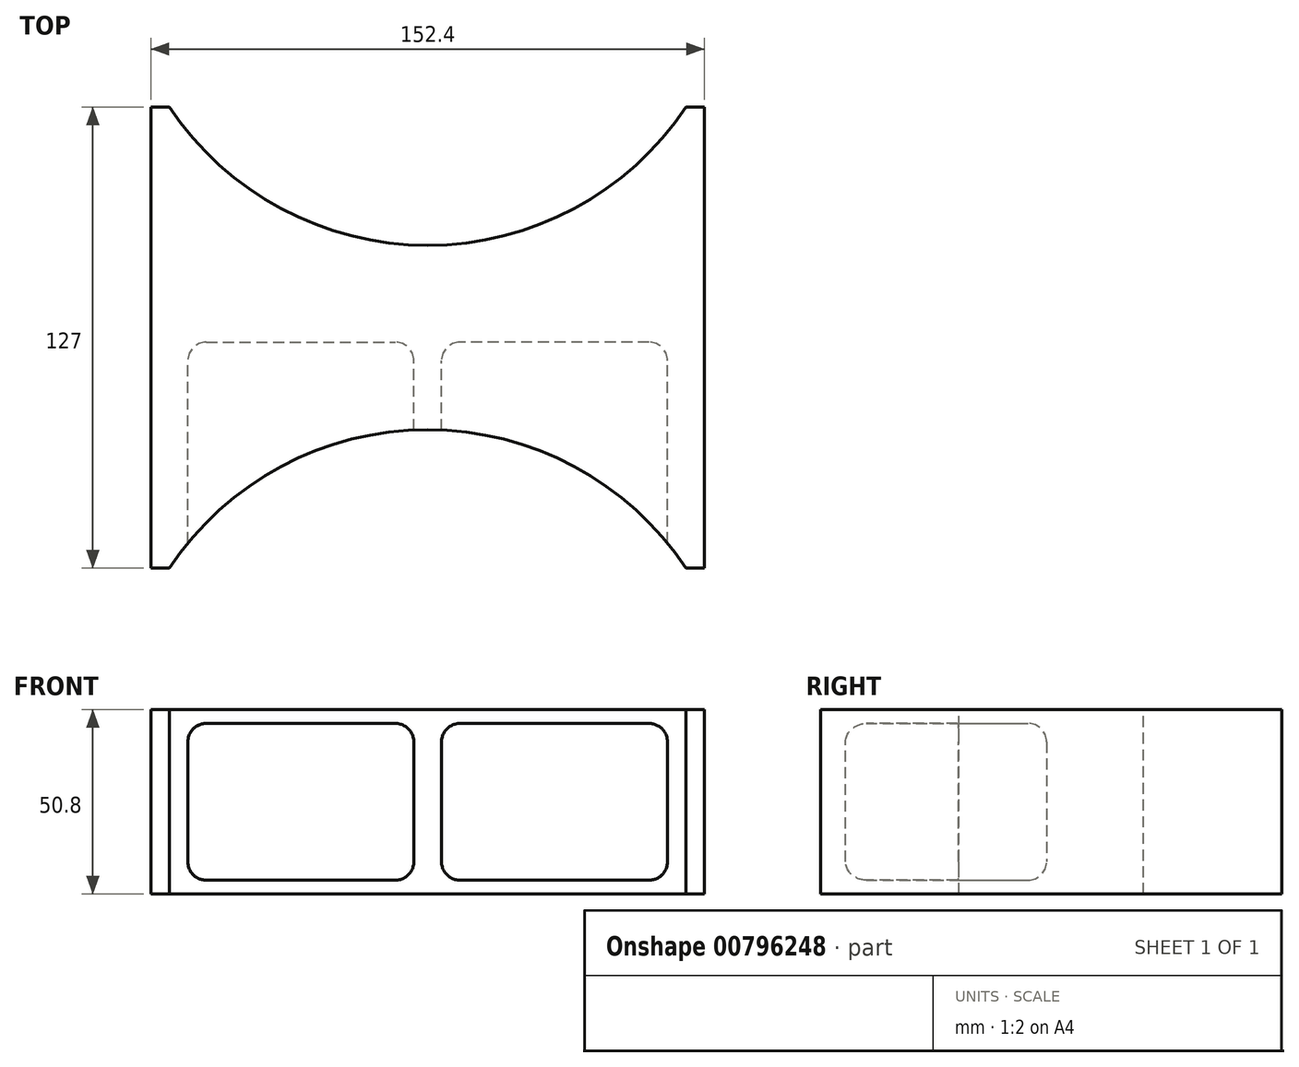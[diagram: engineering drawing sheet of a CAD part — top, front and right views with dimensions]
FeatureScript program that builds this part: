
annotation { "Feature Type Name" : "Feature", "Feature Type Description" : "" }
export const myFeature = defineFeature(function(context is Context, id is Id, definition is map)
    precondition{}
    {
        {
            var Q0;
            Q0=qCreatedBy(makeId("Top.planeOp"),FACE);
            var sketch = newSketch(context, id + "F0", { "sketchPlane" : qUnion([Q0])});
            skLineSegment(sketch, "E0.bottom", {"start": v(76.2, 63.5) * mm, "end": v(-76.2, 63.5) * mm});
            skLineSegment(sketch, "E0.top", {"start": v(76.2, -63.5) * mm, "end": v(-76.2, -63.5) * mm});
            skLineSegment(sketch, "E0.left", {"start": v(76.2, 63.5) * mm, "end": v(76.2, -63.5) * mm});
            skLineSegment(sketch, "E0.right", {"start": v(-76.2, 63.5) * mm, "end": v(-76.2, -63.5) * mm});
            skPoint(sketch, "E0.middle", {"position": v(0, 0) * mm});
            skSolve(sketch);
        }
        {
            var Q0;
            Q0 = qSketchRegion(id + "F0", true);
            extrude(context, id + "F1", {"entities" : qUnion([Q0]), "depth" : 50.8 * mm, "offsetDistance" : 25.4 * mm});
        }
        {
            var Q0;
            Q0=makeQuery(id+"F1.opExtrude","CAP_FACE",FACE,{"disambiguationData":[OSD([sQuery(id+"F0.wireOp",EDGE,"E0.bottom"),sQuery(id+"F0.wireOp",EDGE,"E0.top"),sQuery(id+"F0.wireOp",EDGE,"E0.left"),sQuery(id+"F0.wireOp",EDGE,"E0.right")])],"isStart":false});
            var sketch = newSketch(context, id + "F2", { "sketchPlane" : qUnion([Q0])});
            skArc(sketch, "E1", {"start": v(71.12, -63.5) * mm, "mid": v(0, -25.4) * mm, "end": v(-71.12, -63.5) * mm});
            skArc(sketch, "E2.MirrorCS", {"start": v(71.12, 63.5) * mm, "mid": v(0, 25.4) * mm, "end": v(-71.12, 63.5) * mm});
            skLineSegment(sketch, "E3", {"start": v(-71.12, -63.5) * mm, "end": v(71.12, -63.5) * mm});
            skLineSegment(sketch, "E4", {"start": v(71.12, 63.5) * mm, "end": v(-71.12, 63.5) * mm});
            skSolve(sketch);
        }
        {
            var Q0;
            Q0 = qSketchRegion(id + "F2", true);
            extrude(context, id + "F3", {"entities" : qUnion([Q0]), "operationType" : NewBodyOperationType.REMOVE, "endBound" : BoundingType.THROUGH_ALL, "oppositeDirection" : true, "depth" : 25.4 * mm, "offsetDistance" : 25.4 * mm});
        }
        {
            var Q0;
            Q0=qCreatedBy(makeId("Front.planeOp"),FACE);
            cPlane(context, id + "F4", {"entities" : qUnion([Q0]), "cplaneType" : CPlaneType.OFFSET, "offset" : 1.27 * mm, "width" : 152.4 * mm, "height" : 152.4 * mm});
        }
        {
            var Q0;
            Q0=qCreatedBy(id+"F4.planeOp",FACE);
            var sketch = newSketch(context, id + "F5", { "sketchPlane" : qUnion([Q0])});
            skLineSegment(sketch, "E5.bottom", {"start": v(-66.04, 47) * mm, "end": v(-3.81, 47) * mm});
            skLineSegment(sketch, "E5.top", {"start": v(-66.04, 3.81) * mm, "end": v(-3.8, 3.81) * mm});
            skLineSegment(sketch, "E5.left", {"start": v(-66.04, 47) * mm, "end": v(-66.04, 3.81) * mm});
            skLineSegment(sketch, "E5.right", {"start": v(-3.81, 47) * mm, "end": v(-3.81, 3.81) * mm});
            skLineSegment(sketch, "E6.MirrorCS", {"start": v(66.04, 47) * mm, "end": v(3.81, 47) * mm});
            skLineSegment(sketch, "E7.MirrorCS", {"start": v(3.81, 47) * mm, "end": v(3.81, 3.81) * mm});
            skLineSegment(sketch, "E8.MirrorCS", {"start": v(66.04, 3.81) * mm, "end": v(3.8, 3.81) * mm});
            skLineSegment(sketch, "E9.MirrorCS", {"start": v(66.04, 47) * mm, "end": v(66.04, 3.81) * mm});
            skSolve(sketch);
        }
        {
            var Q0;
            Q0 = qSketchRegion(id + "F5", true);
            extrude(context, id + "F6", {"entities" : qUnion([Q0]), "operationType" : NewBodyOperationType.REMOVE, "endBound" : BoundingType.THROUGH_ALL, "depth" : 25.4 * mm, "offsetDistance" : 25.4 * mm});
        }
        {
            var Q0;
            Q0=makeQuery(id+"F6.boolean.opBoolean","COPY",EDGE,{"derivedFrom":makeQuery(id+"F6.opExtrude","CAP_EDGE",EDGE,{"disambiguationData":[OSD([sQuery(id+"F5.wireOp",EDGE,"E5.right")])],"isStart":true})});
            var Q1;
            Q1=makeQuery(id+"F6.boolean.opBoolean","COPY",EDGE,{"derivedFrom":makeQuery(id+"F6.opExtrude","SWEPT_EDGE",EDGE,{"disambiguationData":[OSD([sQuery(id+"F5.wireOp",EDGE,"E5.top"),sQuery(id+"F5.wireOp",EDGE,"E5.right")])]})});
            var Q2;
            Q2=makeQuery(id+"F6.boolean.opBoolean","COPY",EDGE,{"derivedFrom":makeQuery(id+"F6.opExtrude","CAP_EDGE",EDGE,{"disambiguationData":[OSD([sQuery(id+"F5.wireOp",EDGE,"E5.top")])],"isStart":true})});
            var Q3;
            Q3=makeQuery(id+"F6.boolean.opBoolean","COPY",EDGE,{"derivedFrom":makeQuery(id+"F6.opExtrude","SWEPT_EDGE",EDGE,{"disambiguationData":[OSD([sQuery(id+"F5.wireOp",EDGE,"E5.bottom"),sQuery(id+"F5.wireOp",EDGE,"E5.right")])]})});
            var Q4;
            Q4=makeQuery(id+"F6.boolean.opBoolean","COPY",EDGE,{"derivedFrom":makeQuery(id+"F6.opExtrude","CAP_EDGE",EDGE,{"disambiguationData":[OSD([sQuery(id+"F5.wireOp",EDGE,"E5.bottom")])],"isStart":true})});
            var Q5;
            Q5=makeQuery(id+"F6.boolean.opBoolean","COPY",EDGE,{"derivedFrom":makeQuery(id+"F6.opExtrude","SWEPT_EDGE",EDGE,{"disambiguationData":[OSD([sQuery(id+"F5.wireOp",EDGE,"E5.bottom"),sQuery(id+"F5.wireOp",EDGE,"E5.left")])]})});
            var Q6;
            Q6=makeQuery(id+"F6.boolean.opBoolean","COPY",EDGE,{"derivedFrom":makeQuery(id+"F6.opExtrude","CAP_EDGE",EDGE,{"disambiguationData":[OSD([sQuery(id+"F5.wireOp",EDGE,"E5.left")])],"isStart":true})});
            var Q7;
            Q7=makeQuery(id+"F6.boolean.opBoolean","COPY",EDGE,{"derivedFrom":makeQuery(id+"F6.opExtrude","SWEPT_EDGE",EDGE,{"disambiguationData":[OSD([sQuery(id+"F5.wireOp",EDGE,"E5.top"),sQuery(id+"F5.wireOp",EDGE,"E5.left")])]})});
            var Q8;
            Q8=makeQuery(id+"F6.boolean.opBoolean","COPY",EDGE,{"derivedFrom":makeQuery(id+"F6.opExtrude","CAP_EDGE",EDGE,{"disambiguationData":[OSD([sQuery(id+"F5.wireOp",EDGE,"E8.MirrorCS")])],"isStart":true})});
            var Q9;
            Q9=makeQuery(id+"F6.boolean.opBoolean","COPY",EDGE,{"derivedFrom":makeQuery(id+"F6.opExtrude","SWEPT_EDGE",EDGE,{"disambiguationData":[OSD([sQuery(id+"F5.wireOp",EDGE,"E8.MirrorCS"),sQuery(id+"F5.wireOp",EDGE,"E9.MirrorCS")])]})});
            var Q10;
            Q10=makeQuery(id+"F6.boolean.opBoolean","COPY",EDGE,{"derivedFrom":makeQuery(id+"F6.opExtrude","CAP_EDGE",EDGE,{"disambiguationData":[OSD([sQuery(id+"F5.wireOp",EDGE,"E9.MirrorCS")])],"isStart":true})});
            var Q11;
            Q11=makeQuery(id+"F6.boolean.opBoolean","COPY",EDGE,{"derivedFrom":makeQuery(id+"F6.opExtrude","SWEPT_EDGE",EDGE,{"disambiguationData":[OSD([sQuery(id+"F5.wireOp",EDGE,"E6.MirrorCS"),sQuery(id+"F5.wireOp",EDGE,"E9.MirrorCS")])]})});
            var Q12;
            Q12=makeQuery(id+"F6.boolean.opBoolean","COPY",EDGE,{"derivedFrom":makeQuery(id+"F6.opExtrude","CAP_EDGE",EDGE,{"disambiguationData":[OSD([sQuery(id+"F5.wireOp",EDGE,"E6.MirrorCS")])],"isStart":true})});
            var Q13;
            Q13=makeQuery(id+"F6.boolean.opBoolean","COPY",EDGE,{"derivedFrom":makeQuery(id+"F6.opExtrude","SWEPT_EDGE",EDGE,{"disambiguationData":[OSD([sQuery(id+"F5.wireOp",EDGE,"E6.MirrorCS"),sQuery(id+"F5.wireOp",EDGE,"E7.MirrorCS")])]})});
            var Q14;
            Q14=makeQuery(id+"F6.boolean.opBoolean","COPY",EDGE,{"derivedFrom":makeQuery(id+"F6.opExtrude","CAP_EDGE",EDGE,{"disambiguationData":[OSD([sQuery(id+"F5.wireOp",EDGE,"E7.MirrorCS")])],"isStart":true})});
            var Q15;
            Q15=makeQuery(id+"F6.boolean.opBoolean","COPY",EDGE,{"derivedFrom":makeQuery(id+"F6.opExtrude","SWEPT_EDGE",EDGE,{"disambiguationData":[OSD([sQuery(id+"F5.wireOp",EDGE,"E7.MirrorCS"),sQuery(id+"F5.wireOp",EDGE,"E8.MirrorCS")])]})});
            fillet(context, id + "F7", {"entities" : qUnion([Q0, Q1, Q2, Q3, Q4, Q5, Q6, Q7, Q8, Q9, Q10, Q11, Q12, Q13, Q14, Q15]), "radius" : 5.08 * mm, "tangentPropagation" : true, "allowEdgeOverflow" : false});
        }
    });
